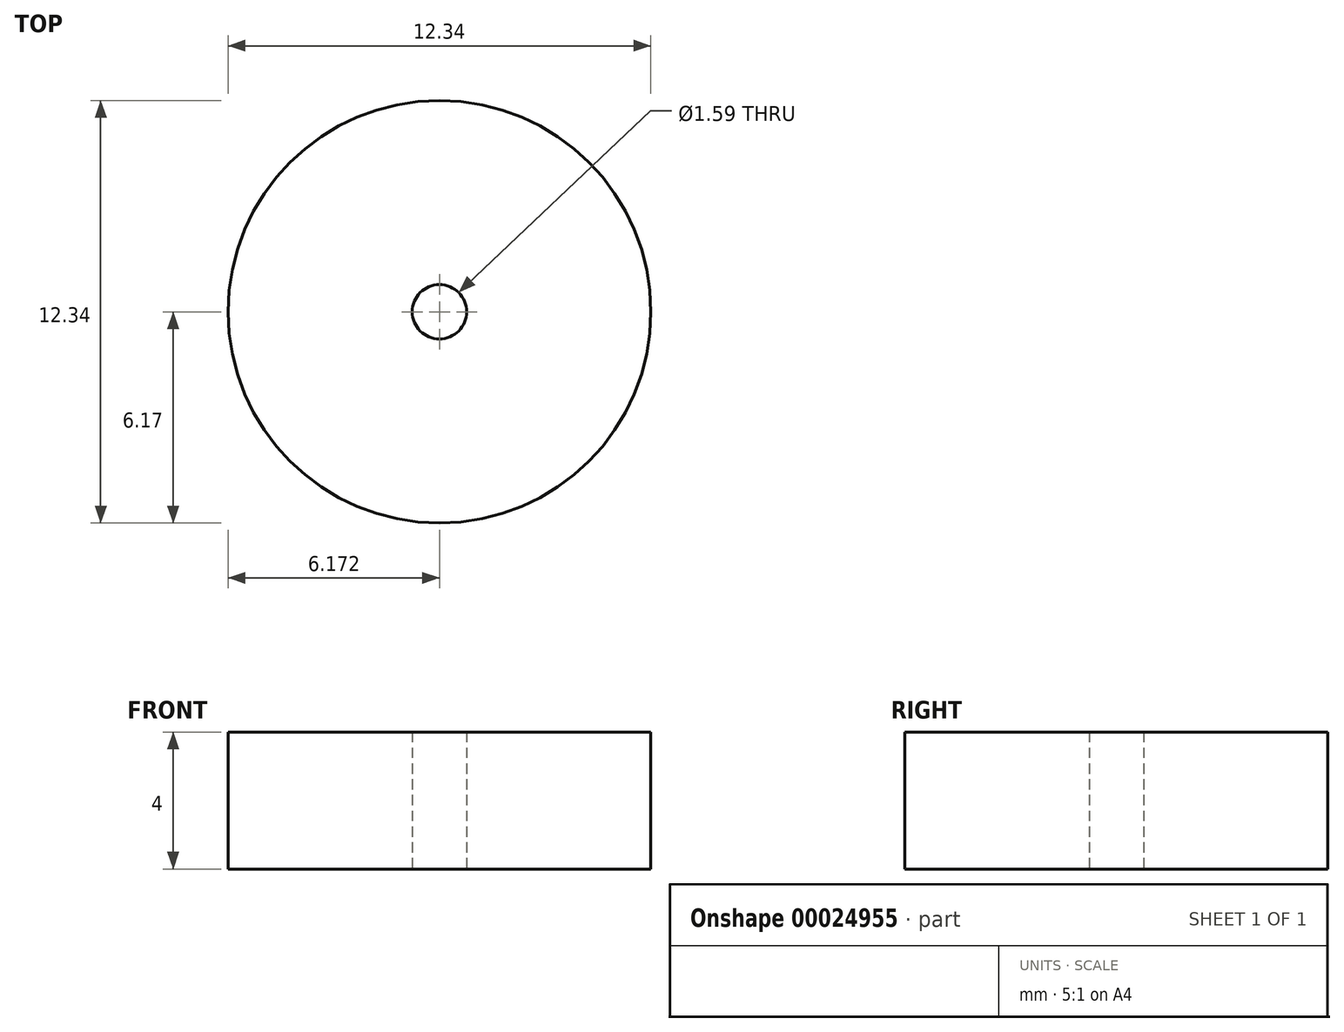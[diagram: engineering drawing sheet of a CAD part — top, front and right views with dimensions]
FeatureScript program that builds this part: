
annotation { "Feature Type Name" : "Feature", "Feature Type Description" : "" }
export const myFeature = defineFeature(function(context is Context, id is Id, definition is map)
    precondition{}
    {
        {
            var Q0;
            Q0=qCreatedBy(makeId("Front.planeOp"),FACE);
            var sketch = newSketch(context, id + "F0", { "sketchPlane" : qUnion([Q0])});
            skLineSegment(sketch, "E0.bottom", {"start": v(-28.77, 16.86) * mm, "end": v(-23.4, 16.86) * mm});
            skLineSegment(sketch, "E0.top", {"start": v(-28.77, 12.86) * mm, "end": v(-23.4, 12.86) * mm});
            skLineSegment(sketch, "E0.left", {"start": v(-28.77, 16.86) * mm, "end": v(-28.77, 12.86) * mm});
            skLineSegment(sketch, "E0.right", {"start": v(-23.4, 16.86) * mm, "end": v(-23.4, 12.86) * mm});
            skLineSegment(sketch, "E1", {"start": v(-22.6, 12.86) * mm, "end": v(-22.6, 22.24) * mm, "construction": true});
            skLineSegment(sketch, "E2.bottom", {"start": v(-23.4, 16.86) * mm, "end": v(-22.6, 16.86) * mm});
            skLineSegment(sketch, "E2.top", {"start": v(-23.4, 12.86) * mm, "end": v(-22.6, 12.86) * mm});
            skLineSegment(sketch, "E2.right", {"start": v(-22.6, 16.86) * mm, "end": v(-22.6, 12.86) * mm});
            skSolve(sketch);
        }
        {
            var Q0;
            Q0=makeQuery(id+"F0.imprint","IMPRINT",FACE,{"disambiguationData":[TD([[makeQuery(id+"F0.imprint","IMPRINT",EDGE,{"derivedFrom":sQuery(id+"F0.wireOp",EDGE,"E0.bottom")}),-1.0]])]});
            var Q1;
            Q1=sQuery(id+"F0.wireOp",EDGE,"E1");
            revolve(context, id + "F1", {"entities" : qUnion([Q0]), "axis" : qUnion([Q1]), "revolveType" : RevolveType.FULL});
        }
    });
